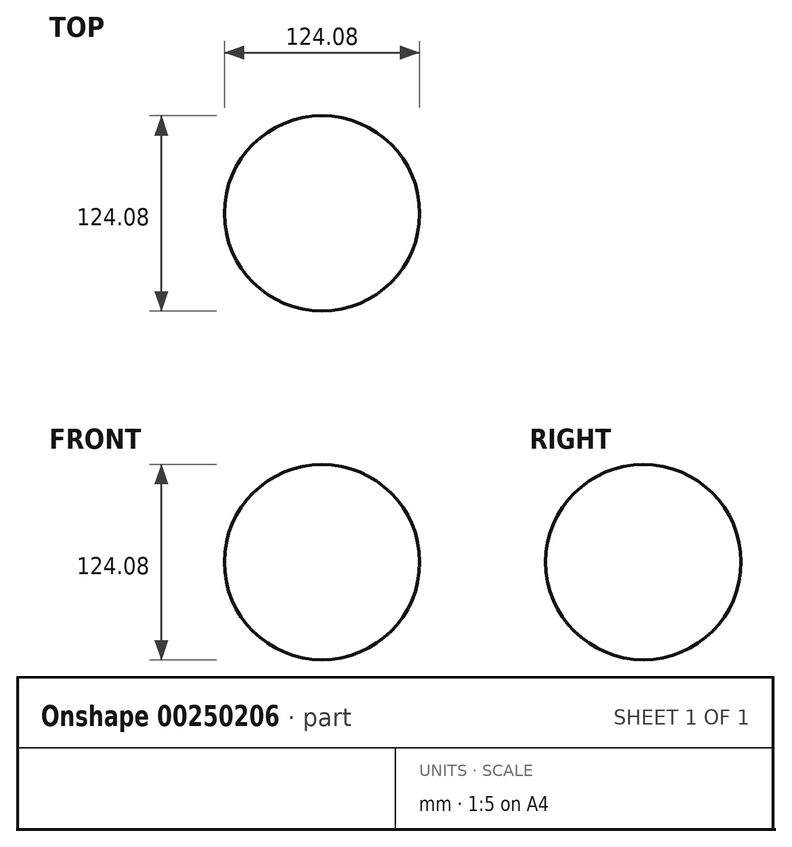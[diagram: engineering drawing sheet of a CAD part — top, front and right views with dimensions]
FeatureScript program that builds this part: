
annotation { "Feature Type Name" : "Feature", "Feature Type Description" : "" }
export const myFeature = defineFeature(function(context is Context, id is Id, definition is map)
    precondition{}
    {
        {
            var Q0;
            Q0=qCreatedBy(makeId("Front.planeOp"),FACE);
            var sketch = newSketch(context, id + "F0", { "sketchPlane" : qUnion([Q0])});
            skArc(sketch, "E0", {"start": v(0, 62.04) * mm, "mid": v(62.04, 0) * mm, "end": v(0, -62.04) * mm});
            skLineSegment(sketch, "E1", {"start": v(0, 62.04) * mm, "end": v(0, -62.04) * mm});
            skSolve(sketch);
        }
        {
            var Q0;
            Q0 = qSketchRegion(id + "F0", true);
            var Q1;
            Q1=sQuery(id+"F0.wireOp",EDGE,"E1");
            revolve(context, id + "F1", {"entities" : qUnion([Q0]), "axis" : qUnion([Q1]), "revolveType" : RevolveType.FULL});
        }
    });
